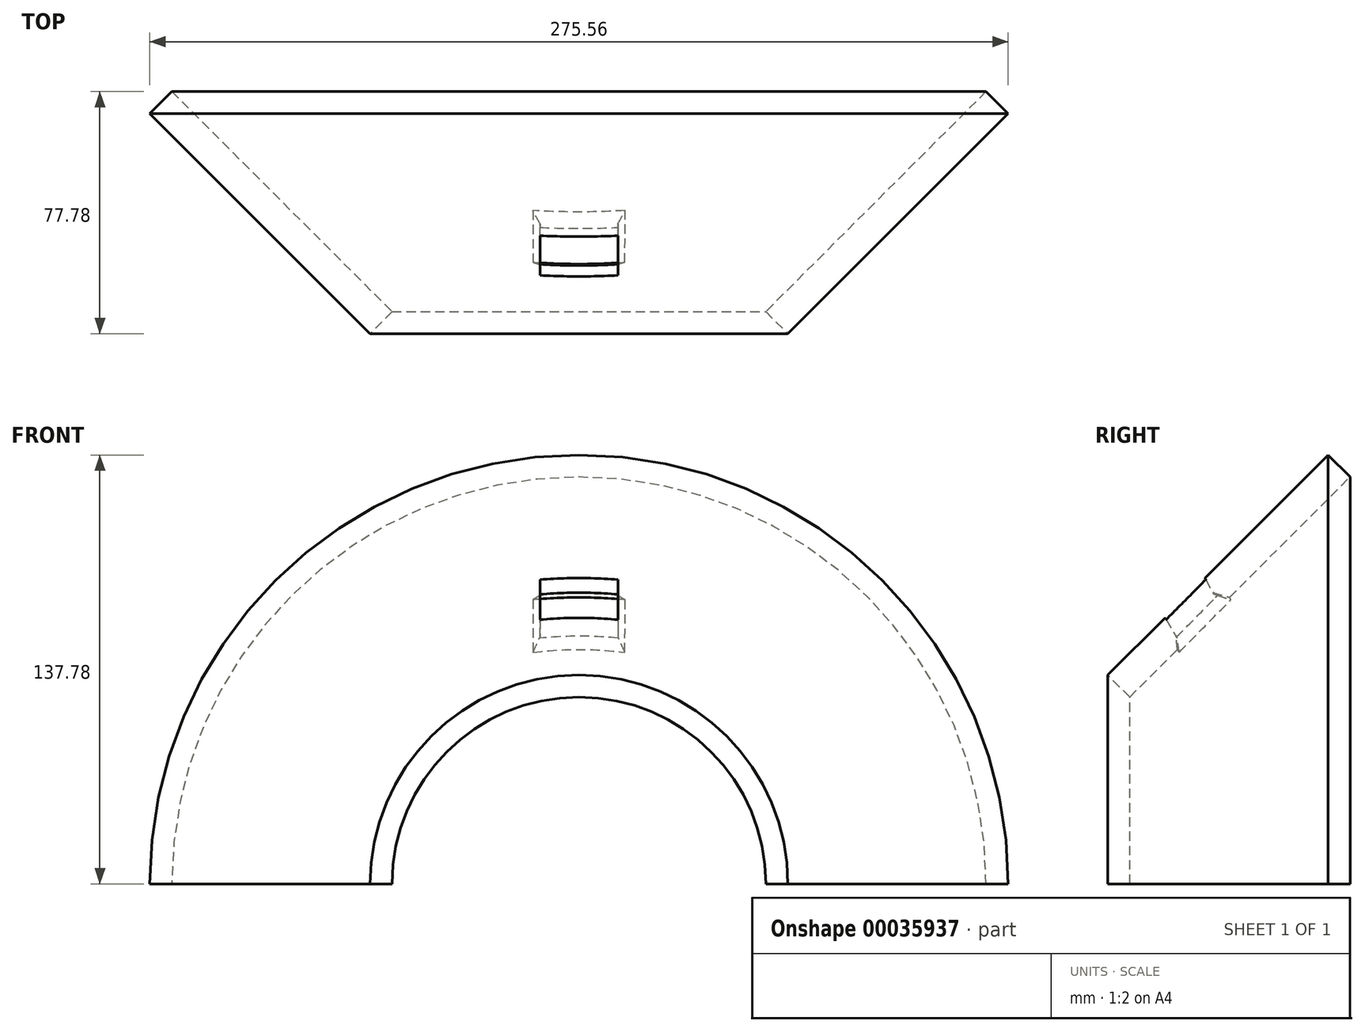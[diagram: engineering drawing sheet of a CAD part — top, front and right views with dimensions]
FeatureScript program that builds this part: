
annotation { "Feature Type Name" : "Feature", "Feature Type Description" : "" }
export const myFeature = defineFeature(function(context is Context, id is Id, definition is map)
    precondition{}
    {
        {
            var Q0;
            Q0=qCreatedBy(makeId("Right.planeOp"),FACE);
            var sketch = newSketch(context, id + "F0", { "sketchPlane" : qUnion([Q0])});
            skLineSegment(sketch, "E0", {"start": v(0, 0) * mm, "end": v(-148.2, 0) * mm, "construction": true});
            skLineSegment(sketch, "E1", {"start": v(0, 130.71) * mm, "end": v(-70.71, 60) * mm});
            skLineSegment(sketch, "E2", {"start": v(-70.71, 60) * mm, "end": v(-77.78, 67.07) * mm});
            skLineSegment(sketch, "E3", {"start": v(-77.78, 67.07) * mm, "end": v(-7.07, 137.78) * mm});
            skLineSegment(sketch, "E4", {"start": v(-7.07, 137.78) * mm, "end": v(0, 130.71) * mm});
            skSolve(sketch);
        }
        {
            var Q0;
            Q0 = qSketchRegion(id + "F0", true);
            var Q1;
            Q1=sQuery(id+"F0.wireOp",EDGE,"E0");
            revolve(context, id + "F1", {"entities" : qUnion([Q0]), "axis" : qUnion([Q1]), "revolveType" : RevolveType.SYMMETRIC, "angle" : 180 * degree});
        }
        {
            var Q0;
            Q0=qCreatedBy(makeId("Right.planeOp"),FACE);
            var sketch = newSketch(context, id + "F2", { "sketchPlane" : qUnion([Q0])});
            skLineSegment(sketch, "E5", {"start": v(-14.95, 25.9) * mm, "end": v(0, 0) * mm, "construction": true});
            skLineSegment(sketch, "E6", {"start": v(0, 0) * mm, "end": v(-15.33, 0) * mm, "construction": true});
            skLineSegment(sketch, "E7", {"start": v(-93.48, 181.9) * mm, "end": v(4.29, 7.43) * mm});
            skLineSegment(sketch, "E8.MirrorCS", {"start": v(-110.8, 171.9) * mm, "end": v(-8.58, 0) * mm});
            skLineSegment(sketch, "E9", {"start": v(-110.8, 171.9) * mm, "end": v(-93.48, 181.9) * mm});
            skLineSegment(sketch, "E10", {"start": v(-8.58, 0) * mm, "end": v(4.29, 7.43) * mm});
            skSolve(sketch);
        }
        {
            var Q0;
            Q0 = qSketchRegion(id + "F2", true);
            extrude(context, id + "F3", {"entities" : qUnion([Q0]), "operationType" : NewBodyOperationType.REMOVE, "endBound" : BoundingType.SYMMETRIC, "oppositeDirection" : true, "depth" : 25 * mm});
        }
        {
            var Q0;
            Q0=makeQuery(id+"F3.boolean.opBoolean","INTERSECT",EDGE,{"derivedFrom":[makeQuery(id+"F1.opRevolve","SWEPT_FACE",FACE,{"disambiguationData":[OSD([sQuery(id+"F0.wireOp",EDGE,"E1")])]}),makeQuery(id+"F3.opExtrude","SWEPT_FACE",FACE,{"disambiguationData":[OSD([sQuery(id+"F2.wireOp",EDGE,"E7")])]})]});
            var Q1;
            Q1=makeQuery(id+"F3.boolean.opBoolean","INTERSECT",EDGE,{"derivedFrom":[makeQuery(id+"F1.opRevolve","SWEPT_FACE",FACE,{"disambiguationData":[OSD([sQuery(id+"F0.wireOp",EDGE,"E1")])]}),makeQuery(id+"F3.opExtrude","CAP_FACE",FACE,{"disambiguationData":[OSD([sQuery(id+"F2.wireOp",EDGE,"E7"),sQuery(id+"F2.wireOp",EDGE,"E8.MirrorCS"),sQuery(id+"F2.wireOp",EDGE,"E9"),sQuery(id+"F2.wireOp",EDGE,"E10")])],"isStart":true})]});
            var Q2;
            Q2=makeQuery(id+"F3.boolean.opBoolean","INTERSECT",EDGE,{"derivedFrom":[makeQuery(id+"F1.opRevolve","SWEPT_FACE",FACE,{"disambiguationData":[OSD([sQuery(id+"F0.wireOp",EDGE,"E1")])]}),makeQuery(id+"F3.opExtrude","SWEPT_FACE",FACE,{"disambiguationData":[OSD([sQuery(id+"F2.wireOp",EDGE,"E8.MirrorCS")])]})]});
            var Q3;
            Q3=makeQuery(id+"F3.boolean.opBoolean","INTERSECT",EDGE,{"derivedFrom":[makeQuery(id+"F1.opRevolve","SWEPT_FACE",FACE,{"disambiguationData":[OSD([sQuery(id+"F0.wireOp",EDGE,"E1")])]}),makeQuery(id+"F3.opExtrude","CAP_FACE",FACE,{"disambiguationData":[OSD([sQuery(id+"F2.wireOp",EDGE,"E7"),sQuery(id+"F2.wireOp",EDGE,"E8.MirrorCS"),sQuery(id+"F2.wireOp",EDGE,"E9"),sQuery(id+"F2.wireOp",EDGE,"E10")])],"isStart":false})]});
            chamfer(context, id + "F4", {"entities" : qUnion([Q0, Q1, Q2, Q3]), "chamferType" : ChamferType.OFFSET_ANGLE, "width" : 5 * mm, "oppositeDirection" : false, "angle" : 45 * degree, "tangentPropagation" : true});
        }
    });
